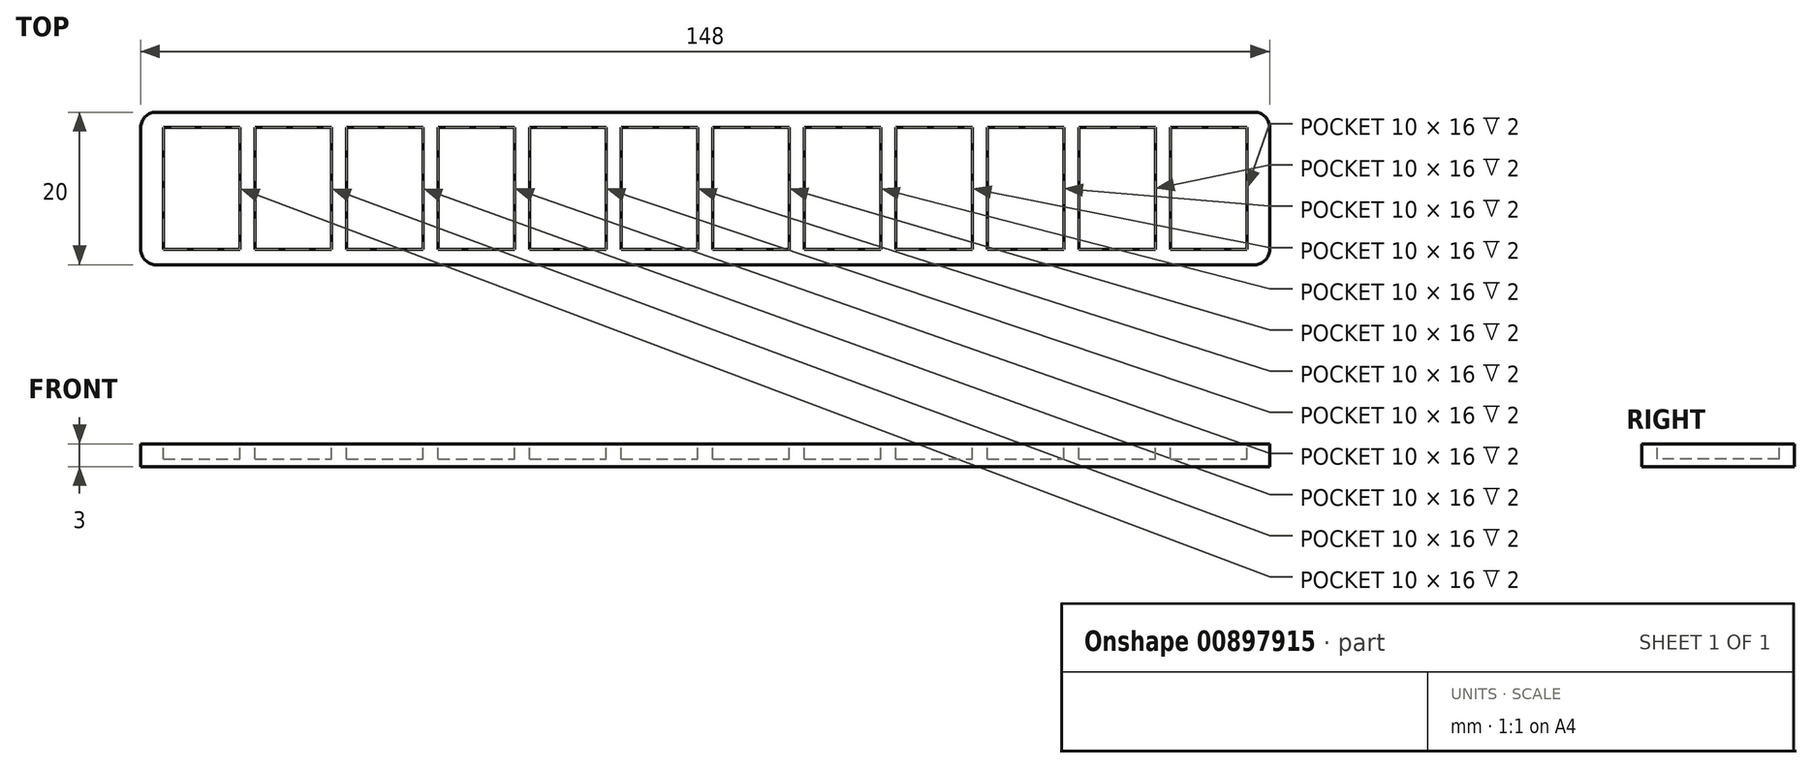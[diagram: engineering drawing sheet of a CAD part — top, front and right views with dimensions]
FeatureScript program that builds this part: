
annotation { "Feature Type Name" : "Feature", "Feature Type Description" : "" }
export const myFeature = defineFeature(function(context is Context, id is Id, definition is map)
    precondition{}
    {
        {
            var Q0;
            Q0=qCreatedBy(makeId("Top.planeOp"),FACE);
            var sketch = newSketch(context, id + "F0", { "sketchPlane" : qUnion([Q0])});
            skLineSegment(sketch, "E0.bottom", {"start": v(-75.02, 10.45) * mm, "end": v(72.98, 10.45) * mm});
            skLineSegment(sketch, "E0.top", {"start": v(-75.02, -9.55) * mm, "end": v(72.98, -9.55) * mm});
            skLineSegment(sketch, "E0.left", {"start": v(-75.02, 10.45) * mm, "end": v(-75.02, -9.55) * mm});
            skLineSegment(sketch, "E0.right", {"start": v(72.98, 10.45) * mm, "end": v(72.98, -9.55) * mm});
            skLineSegment(sketch, "E1", {"start": v(-1.02, 10.45) * mm, "end": v(-1.02, -9.55) * mm, "construction": true});
            skSolve(sketch);
        }
        {
            var Q0;
            Q0=qSketchRegion(id+"F0",true);
            extrude(context, id + "F1", {"entities" : qUnion([Q0]), "depth" : 3 * mm, "offsetDistance" : 25 * mm});
        }
        {
            var Q0;
            Q0=makeQuery(id+"F1.opExtrude","CAP_FACE",FACE,{"disambiguationData":[OSD([sQuery(id+"F0.wireOp",EDGE,"E0.bottom"),sQuery(id+"F0.wireOp",EDGE,"E0.top"),sQuery(id+"F0.wireOp",EDGE,"E0.left"),sQuery(id+"F0.wireOp",EDGE,"E0.right")])],"isStart":false});
            var sketch = newSketch(context, id + "F2", { "sketchPlane" : qUnion([Q0])});
            skLineSegment(sketch, "E2.bottom", {"start": v(-72.02, 8.45) * mm, "end": v(-62.02, 8.45) * mm});
            skLineSegment(sketch, "E2.top", {"start": v(-72.02, -7.55) * mm, "end": v(-62.02, -7.55) * mm});
            skLineSegment(sketch, "E2.left", {"start": v(-72.02, 8.45) * mm, "end": v(-72.02, -7.55) * mm});
            skLineSegment(sketch, "E2.right", {"start": v(-62.02, 8.45) * mm, "end": v(-62.02, -7.55) * mm});
            skLineSegment(sketch, "E3.1.0.0", {"start": v(-60.02, 8.45) * mm, "end": v(-60.02, -7.55) * mm});
            skLineSegment(sketch, "E3.1.0.1", {"start": v(-60.02, 8.45) * mm, "end": v(-50.02, 8.45) * mm});
            skLineSegment(sketch, "E3.1.0.2", {"start": v(-60.02, -7.55) * mm, "end": v(-50.02, -7.55) * mm});
            skLineSegment(sketch, "E3.1.0.3", {"start": v(-50.02, 8.45) * mm, "end": v(-50.02, -7.55) * mm});
            skLineSegment(sketch, "E3.2.0.0", {"start": v(-48.02, 8.45) * mm, "end": v(-48.02, -7.55) * mm});
            skLineSegment(sketch, "E3.2.0.1", {"start": v(-48.02, 8.45) * mm, "end": v(-38.02, 8.45) * mm});
            skLineSegment(sketch, "E3.2.0.2", {"start": v(-48.02, -7.55) * mm, "end": v(-38.02, -7.55) * mm});
            skLineSegment(sketch, "E3.2.0.3", {"start": v(-38.02, 8.45) * mm, "end": v(-38.02, -7.55) * mm});
            skLineSegment(sketch, "E3.3.0.0", {"start": v(-36.02, 8.45) * mm, "end": v(-36.02, -7.55) * mm});
            skLineSegment(sketch, "E3.3.0.1", {"start": v(-36.02, 8.45) * mm, "end": v(-26.02, 8.45) * mm});
            skLineSegment(sketch, "E3.3.0.2", {"start": v(-36.02, -7.55) * mm, "end": v(-26.02, -7.55) * mm});
            skLineSegment(sketch, "E3.3.0.3", {"start": v(-26.02, 8.45) * mm, "end": v(-26.02, -7.55) * mm});
            skLineSegment(sketch, "E3.4.0.0", {"start": v(-24.02, 8.45) * mm, "end": v(-24.02, -7.55) * mm});
            skLineSegment(sketch, "E3.4.0.1", {"start": v(-24.02, 8.45) * mm, "end": v(-14.02, 8.45) * mm});
            skLineSegment(sketch, "E3.4.0.2", {"start": v(-24.02, -7.55) * mm, "end": v(-14.02, -7.55) * mm});
            skLineSegment(sketch, "E3.4.0.3", {"start": v(-14.02, 8.45) * mm, "end": v(-14.02, -7.55) * mm});
            skLineSegment(sketch, "E3.5.0.0", {"start": v(-12.02, 8.45) * mm, "end": v(-12.02, -7.55) * mm});
            skLineSegment(sketch, "E3.5.0.1", {"start": v(-12.02, 8.45) * mm, "end": v(-2.02, 8.45) * mm});
            skLineSegment(sketch, "E3.5.0.2", {"start": v(-12.02, -7.55) * mm, "end": v(-2.02, -7.55) * mm});
            skLineSegment(sketch, "E3.5.0.3", {"start": v(-2.02, 8.45) * mm, "end": v(-2.02, -7.55) * mm});
            skLineSegment(sketch, "E3.6.0.0", {"start": v(-0.02, 8.45) * mm, "end": v(-0.02, -7.55) * mm});
            skLineSegment(sketch, "E3.6.0.1", {"start": v(-0.02, 8.45) * mm, "end": v(9.98, 8.45) * mm});
            skLineSegment(sketch, "E3.6.0.2", {"start": v(-0.02, -7.55) * mm, "end": v(9.98, -7.55) * mm});
            skLineSegment(sketch, "E3.6.0.3", {"start": v(9.98, 8.45) * mm, "end": v(9.98, -7.55) * mm});
            skLineSegment(sketch, "E3.7.0.0", {"start": v(11.98, 8.45) * mm, "end": v(11.98, -7.55) * mm});
            skLineSegment(sketch, "E3.7.0.1", {"start": v(11.98, 8.45) * mm, "end": v(21.98, 8.45) * mm});
            skLineSegment(sketch, "E3.7.0.2", {"start": v(11.98, -7.55) * mm, "end": v(21.98, -7.55) * mm});
            skLineSegment(sketch, "E3.7.0.3", {"start": v(21.98, 8.45) * mm, "end": v(21.98, -7.55) * mm});
            skLineSegment(sketch, "E3.8.0.0", {"start": v(23.98, 8.45) * mm, "end": v(23.98, -7.55) * mm});
            skLineSegment(sketch, "E3.8.0.1", {"start": v(23.98, 8.45) * mm, "end": v(33.98, 8.45) * mm});
            skLineSegment(sketch, "E3.8.0.2", {"start": v(23.98, -7.55) * mm, "end": v(33.98, -7.55) * mm});
            skLineSegment(sketch, "E3.8.0.3", {"start": v(33.98, 8.45) * mm, "end": v(33.98, -7.55) * mm});
            skLineSegment(sketch, "E3.9.0.0", {"start": v(35.98, 8.45) * mm, "end": v(35.98, -7.55) * mm});
            skLineSegment(sketch, "E3.9.0.1", {"start": v(35.98, 8.45) * mm, "end": v(45.98, 8.45) * mm});
            skLineSegment(sketch, "E3.9.0.2", {"start": v(35.98, -7.55) * mm, "end": v(45.98, -7.55) * mm});
            skLineSegment(sketch, "E3.9.0.3", {"start": v(45.98, 8.45) * mm, "end": v(45.98, -7.55) * mm});
            skLineSegment(sketch, "E3.10.0.0", {"start": v(47.98, 8.45) * mm, "end": v(47.98, -7.55) * mm});
            skLineSegment(sketch, "E3.10.0.1", {"start": v(47.98, 8.45) * mm, "end": v(57.98, 8.45) * mm});
            skLineSegment(sketch, "E3.10.0.2", {"start": v(47.98, -7.55) * mm, "end": v(57.98, -7.55) * mm});
            skLineSegment(sketch, "E3.10.0.3", {"start": v(57.98, 8.45) * mm, "end": v(57.98, -7.55) * mm});
            skLineSegment(sketch, "E3.11.0.0", {"start": v(59.98, 8.45) * mm, "end": v(59.98, -7.55) * mm});
            skLineSegment(sketch, "E3.11.0.1", {"start": v(59.98, 8.45) * mm, "end": v(69.98, 8.45) * mm});
            skLineSegment(sketch, "E3.11.0.2", {"start": v(59.98, -7.55) * mm, "end": v(69.98, -7.55) * mm});
            skLineSegment(sketch, "E3.11.0.3", {"start": v(69.98, 8.45) * mm, "end": v(69.98, -7.55) * mm});
            skLineSegment(sketch, "E3.direction1", {"start": v(-72.02, -7.55) * mm, "end": v(-60.02, -7.55) * mm, "construction": true});
            skSolve(sketch);
        }
        {
            var Q0;
            Q0=qSketchRegion(id+"F2",true);
            extrude(context, id + "F3", {"entities" : qUnion([Q0]), "operationType" : NewBodyOperationType.REMOVE, "oppositeDirection" : true, "depth" : 2 * mm, "offsetDistance" : 25 * mm});
        }
        {
            var Q0;
            Q0=makeQuery(id+"F1.opExtrude","SWEPT_EDGE",EDGE,{"disambiguationData":[OSD([sQuery(id+"F0.wireOp",EDGE,"E0.top"),sQuery(id+"F0.wireOp",EDGE,"E0.left")])]});
            var Q1;
            Q1=makeQuery(id+"F1.opExtrude","SWEPT_EDGE",EDGE,{"disambiguationData":[OSD([sQuery(id+"F0.wireOp",EDGE,"E0.top"),sQuery(id+"F0.wireOp",EDGE,"E0.right")])]});
            var Q2;
            Q2=makeQuery(id+"F1.opExtrude","SWEPT_EDGE",EDGE,{"disambiguationData":[OSD([sQuery(id+"F0.wireOp",EDGE,"E0.bottom"),sQuery(id+"F0.wireOp",EDGE,"E0.right")])]});
            var Q3;
            Q3=makeQuery(id+"F1.opExtrude","SWEPT_EDGE",EDGE,{"disambiguationData":[OSD([sQuery(id+"F0.wireOp",EDGE,"E0.bottom"),sQuery(id+"F0.wireOp",EDGE,"E0.left")])]});
            var Q4;
            Q4=makeQuery(id+"F3.boolean.opBoolean","COPY",EDGE,{"derivedFrom":makeQuery(id+"F3.opExtrude","CAP_EDGE",EDGE,{"disambiguationData":[OSD([sQuery(id+"F2.wireOp",EDGE,"E2.left")])],"isStart":true})});
            var Q5;
            Q5=makeQuery(id+"F3.boolean.opBoolean","COPY",EDGE,{"derivedFrom":makeQuery(id+"F3.opExtrude","CAP_EDGE",EDGE,{"disambiguationData":[OSD([sQuery(id+"F2.wireOp",EDGE,"E3.1.0.0")])],"isStart":true})});
            var Q6;
            Q6=makeQuery(id+"F3.boolean.opBoolean","COPY",EDGE,{"derivedFrom":makeQuery(id+"F3.opExtrude","CAP_EDGE",EDGE,{"disambiguationData":[OSD([sQuery(id+"F2.wireOp",EDGE,"E3.2.0.0")])],"isStart":true})});
            var Q7;
            Q7=makeQuery(id+"F3.boolean.opBoolean","COPY",EDGE,{"derivedFrom":makeQuery(id+"F3.opExtrude","CAP_EDGE",EDGE,{"disambiguationData":[OSD([sQuery(id+"F2.wireOp",EDGE,"E3.3.0.0")])],"isStart":true})});
            var Q8;
            Q8=makeQuery(id+"F3.boolean.opBoolean","COPY",EDGE,{"derivedFrom":makeQuery(id+"F3.opExtrude","CAP_EDGE",EDGE,{"disambiguationData":[OSD([sQuery(id+"F2.wireOp",EDGE,"E3.4.0.0")])],"isStart":true})});
            var Q9;
            Q9=makeQuery(id+"F3.boolean.opBoolean","COPY",EDGE,{"derivedFrom":makeQuery(id+"F3.opExtrude","CAP_EDGE",EDGE,{"disambiguationData":[OSD([sQuery(id+"F2.wireOp",EDGE,"E3.5.0.0")])],"isStart":true})});
            var Q10;
            Q10=makeQuery(id+"F3.boolean.opBoolean","COPY",EDGE,{"derivedFrom":makeQuery(id+"F3.opExtrude","CAP_EDGE",EDGE,{"disambiguationData":[OSD([sQuery(id+"F2.wireOp",EDGE,"E3.6.0.0")])],"isStart":true})});
            var Q11;
            Q11=makeQuery(id+"F3.boolean.opBoolean","COPY",EDGE,{"derivedFrom":makeQuery(id+"F3.opExtrude","CAP_EDGE",EDGE,{"disambiguationData":[OSD([sQuery(id+"F2.wireOp",EDGE,"E3.7.0.0")])],"isStart":true})});
            var Q12;
            Q12=makeQuery(id+"F3.boolean.opBoolean","COPY",EDGE,{"derivedFrom":makeQuery(id+"F3.opExtrude","CAP_EDGE",EDGE,{"disambiguationData":[OSD([sQuery(id+"F2.wireOp",EDGE,"E3.8.0.0")])],"isStart":true})});
            var Q13;
            Q13=makeQuery(id+"F3.boolean.opBoolean","COPY",EDGE,{"derivedFrom":makeQuery(id+"F3.opExtrude","CAP_EDGE",EDGE,{"disambiguationData":[OSD([sQuery(id+"F2.wireOp",EDGE,"E3.9.0.0")])],"isStart":true})});
            var Q14;
            Q14=makeQuery(id+"F3.boolean.opBoolean","COPY",EDGE,{"derivedFrom":makeQuery(id+"F3.opExtrude","CAP_EDGE",EDGE,{"disambiguationData":[OSD([sQuery(id+"F2.wireOp",EDGE,"E3.10.0.0")])],"isStart":true})});
            var Q15;
            Q15=makeQuery(id+"F3.boolean.opBoolean","COPY",EDGE,{"derivedFrom":makeQuery(id+"F3.opExtrude","CAP_EDGE",EDGE,{"disambiguationData":[OSD([sQuery(id+"F2.wireOp",EDGE,"E3.11.0.0")])],"isStart":true})});
            fillet(context, id + "F4", {"entities" : qUnion([Q0, Q1, Q2, Q3, Q4, Q5, Q6, Q7, Q8, Q9, Q10, Q11, Q12, Q13, Q14, Q15]), "radius" : 2 * mm, "tangentPropagation" : true, "allowEdgeOverflow" : false});
        }
    });
